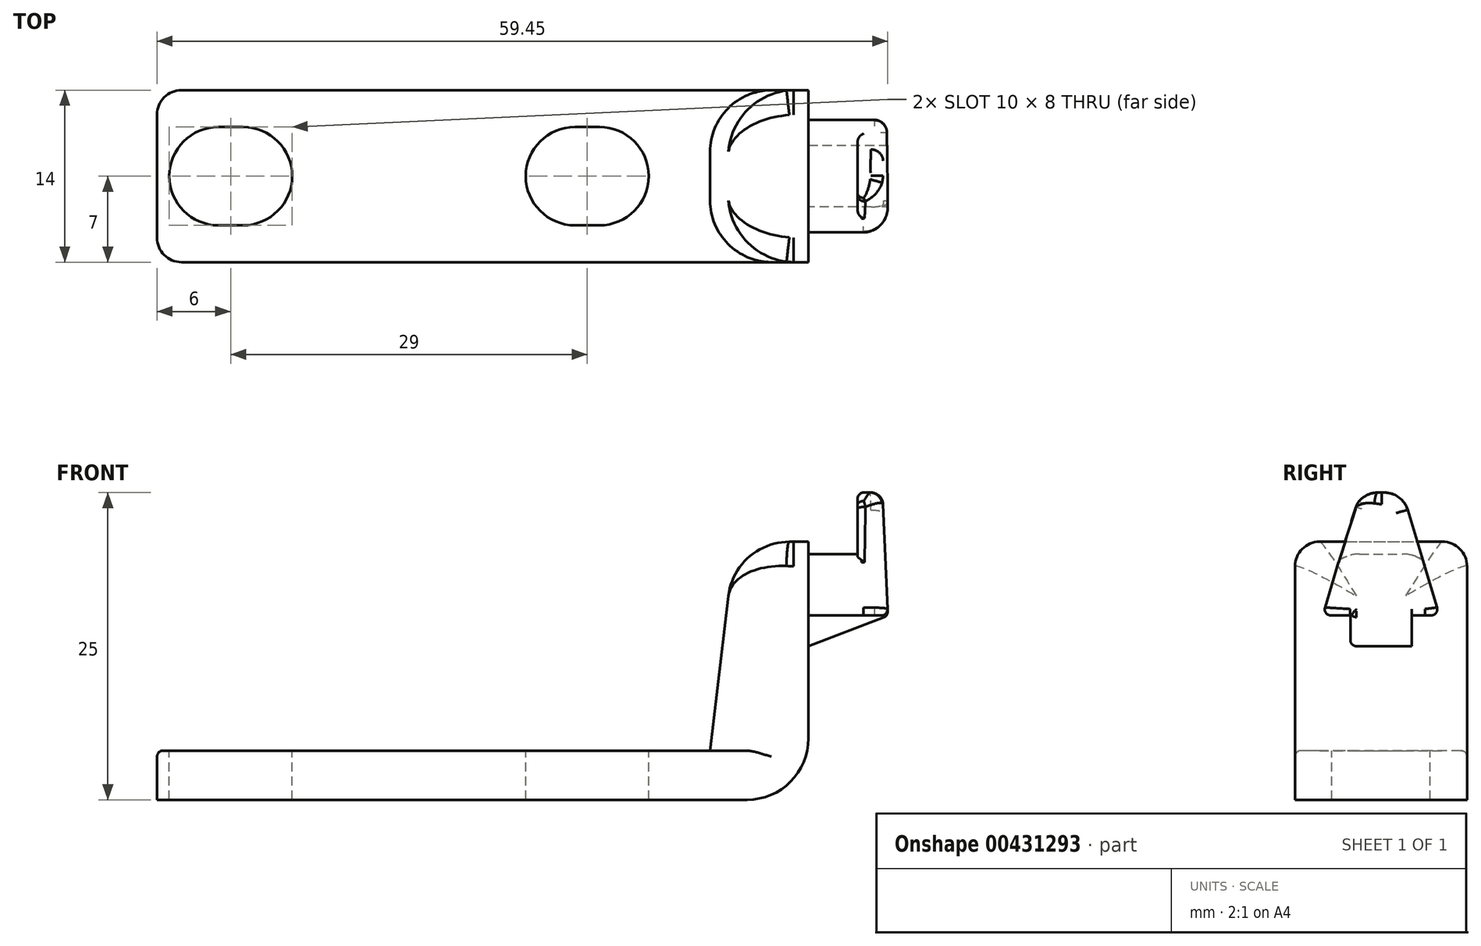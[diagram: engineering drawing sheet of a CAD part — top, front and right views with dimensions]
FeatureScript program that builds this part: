
annotation { "Feature Type Name" : "Feature", "Feature Type Description" : "" }
export const myFeature = defineFeature(function(context is Context, id is Id, definition is map)
    precondition{}
    {
        {
            var Q0;
            Q0=qCreatedBy(makeId("Front.planeOp"),FACE);
            var sketch = newSketch(context, id + "F0", { "sketchPlane" : qUnion([Q0])});
            skLineSegment(sketch, "E0.bottom", {"start": v(-32.49, -4) * mm, "end": v(20.51, -4) * mm});
            skLineSegment(sketch, "E0.top", {"start": v(-32.49, 0) * mm, "end": v(20.51, 0) * mm});
            skLineSegment(sketch, "E0.left", {"start": v(-32.49, -4) * mm, "end": v(-32.49, 0) * mm});
            skLineSegment(sketch, "E0.right", {"start": v(20.51, -4) * mm, "end": v(20.51, 0) * mm});
            skLineSegment(sketch, "E1", {"start": v(20.51, 0) * mm, "end": v(20.51, 17) * mm});
            skLineSegment(sketch, "E2", {"start": v(20.51, 17) * mm, "end": v(14.51, 17) * mm});
            skLineSegment(sketch, "E3", {"start": v(14.51, 17) * mm, "end": v(12.51, 0) * mm});
            skLineSegment(sketch, "E4", {"start": v(12.51, 0) * mm, "end": v(20.51, 0) * mm});
            skLineSegment(sketch, "E5.bottom", {"start": v(20.51, 16) * mm, "end": v(24.51, 16) * mm});
            skLineSegment(sketch, "E5.top", {"start": v(20.51, 11) * mm, "end": v(24.51, 11) * mm});
            skLineSegment(sketch, "E5.left", {"start": v(20.51, 16) * mm, "end": v(20.51, 11) * mm});
            skLineSegment(sketch, "E5.right", {"start": v(24.51, 16) * mm, "end": v(24.51, 11) * mm});
            skLineSegment(sketch, "E6.bottom", {"start": v(24.51, 11) * mm, "end": v(27.01, 11) * mm});
            skLineSegment(sketch, "E6.top", {"start": v(24.51, 21) * mm, "end": v(27.01, 21) * mm});
            skLineSegment(sketch, "E6.left", {"start": v(24.51, 11) * mm, "end": v(24.51, 21) * mm});
            skLineSegment(sketch, "E6.right", {"start": v(27.01, 11) * mm, "end": v(27.01, 21) * mm});
            skArc(sketch, "E7", {"start": v(27.01, 11) * mm, "mid": v(26.28, 9.23) * mm, "end": v(24.51, 8.5) * mm});
            skLineSegment(sketch, "E8", {"start": v(24.51, 8.5) * mm, "end": v(20.51, 8.5) * mm});
            skSolve(sketch);
        }
        {
            var Q0;
            {var subQ0=sQuery(id+"F0.wireOp",EDGE,"E2");Q0=makeQuery(id+"F0.imprint","IMPRINT",FACE,{"disambiguationData":[TD([[makeQuery(id+"F0.imprint","IMPRINT",EDGE,{"derivedFrom":subQ0}),1.0]])]});}
            var Q1;
            Q1=makeQuery(id+"F0.imprint","IMPRINT",FACE,{"disambiguationData":[TD([[makeQuery(id+"F0.imprint","IMPRINT",EDGE,{"derivedFrom":sQuery(id+"F0.wireOp",EDGE,"E0.bottom")}),1.0]])]});
            extrude(context, id + "F1", {"entities" : qUnion([Q0, Q1]), "endBound" : BoundingType.SYMMETRIC, "depth" : 14 * mm, "offsetDistance" : 25 * mm});
        }
        {
            var Q0;
            {var subQ0=sQuery(id+"F0.wireOp",EDGE,"E5.bottom");Q0=makeQuery(id+"F0.imprint","IMPRINT",FACE,{"disambiguationData":[TD([[makeQuery(id+"F0.imprint","IMPRINT",EDGE,{"derivedFrom":subQ0}),-1.0]])]});}
            extrude(context, id + "F2", {"entities" : qUnion([Q0]), "operationType" : NewBodyOperationType.ADD, "endBound" : BoundingType.SYMMETRIC, "depth" : 9.5 * mm, "offsetDistance" : 25 * mm});
        }
        {
            var Q0;
            {var subQ3=sQuery(id+"F0.wireOp",EDGE,"E6.bottom");Q0=makeQuery(id+"F0.imprint","IMPRINT",FACE,{"disambiguationData":[TD([[makeQuery(id+"F0.imprint","IMPRINT",EDGE,{"derivedFrom":subQ3}),1.0]])]});}
            extrude(context, id + "F3", {"entities" : qUnion([Q0]), "operationType" : NewBodyOperationType.ADD, "endBound" : BoundingType.SYMMETRIC, "depth" : 9.5 * mm, "offsetDistance" : 25 * mm});
        }
        {
            var Q0;
            {var subQ0=sQuery(id+"F0.wireOp",EDGE,"E5.top");Q0=makeQuery(id+"F0.imprint","IMPRINT",FACE,{"disambiguationData":[TD([[makeQuery(id+"F0.imprint","IMPRINT",EDGE,{"derivedFrom":subQ0}),-1.0]])]});}
            extrude(context, id + "F4", {"entities" : qUnion([Q0]), "operationType" : NewBodyOperationType.ADD, "endBound" : BoundingType.SYMMETRIC, "depth" : 5 * mm, "offsetDistance" : 25 * mm});
        }
        {
            var Q0;
            Q0=makeQuery(id+"F1.opExtrude","CAP_EDGE",EDGE,{"disambiguationData":[OSD([sQuery(id+"F0.wireOp",EDGE,"E0.left")])],"isStart":true});
            var Q1;
            Q1=makeQuery(id+"F1.opExtrude","CAP_EDGE",EDGE,{"disambiguationData":[OSD([sQuery(id+"F0.wireOp",EDGE,"E0.left")])],"isStart":false});
            fillet(context, id + "F5", {"entities" : qUnion([Q0, Q1]), "radius" : 2 * mm, "tangentPropagation" : true, "allowEdgeOverflow" : false});
        }
        {
            var Q0;
            Q0=makeQuery(id+"F1.opExtrude","CAP_EDGE",EDGE,{"disambiguationData":[OSD([sQuery(id+"F0.wireOp",EDGE,"E2")])],"isStart":true});
            var Q1;
            Q1=makeQuery(id+"F1.opExtrude","CAP_EDGE",EDGE,{"disambiguationData":[OSD([sQuery(id+"F0.wireOp",EDGE,"E2")])],"isStart":false});
            fillet(context, id + "F6", {"entities" : qUnion([Q0, Q1]), "radius" : 2 * mm, "tangentPropagation" : true, "allowEdgeOverflow" : false});
        }
        {
            var Q0;
            Q0=makeQuery(id+"F2.opExtrude","CAP_EDGE",EDGE,{"disambiguationData":[OSD([sQuery(id+"F0.wireOp",EDGE,"E5.bottom")])],"isStart":true});
            var Q1;
            Q1=makeQuery(id+"F2.opExtrude","CAP_EDGE",EDGE,{"disambiguationData":[OSD([sQuery(id+"F0.wireOp",EDGE,"E5.bottom")])],"isStart":false});
            fillet(context, id + "F7", {"entities" : qUnion([Q0, Q1]), "radius" : 3 * mm, "tangentPropagation" : true, "allowEdgeOverflow" : false});
        }
        {
            var Q0;
            Q0=makeQuery(id+"F3.opExtrude","CAP_EDGE",EDGE,{"disambiguationData":[OSD([sQuery(id+"F0.wireOp",EDGE,"E6.top")])],"isStart":false});
            var Q1;
            Q1=makeQuery(id+"F3.opExtrude","CAP_EDGE",EDGE,{"disambiguationData":[OSD([sQuery(id+"F0.wireOp",EDGE,"E6.top")])],"isStart":true});
            fillet(context, id + "F8", {"entities" : qUnion([Q0, Q1]), "radius" : 3 * mm, "tangentPropagation" : true, "allowEdgeOverflow" : false});
        }
        {
            var Q0;
            Q0=qCreatedBy(makeId("Top.planeOp"),FACE);
            var sketch = newSketch(context, id + "F9", { "sketchPlane" : qUnion([Q0])});
            skLineSegment(sketch, "E9", {"start": v(1.51, 0) * mm, "end": v(3.51, 0) * mm});
            skArc(sketch, "E10.0.startCap", {"start": v(1.51, -4) * mm, "mid": v(-2.49, 0) * mm, "end": v(1.51, 4) * mm});
            skArc(sketch, "E10.0.endCap", {"start": v(3.51, 4) * mm, "mid": v(7.51, 0) * mm, "end": v(3.51, -4) * mm});
            skLineSegment(sketch, "E10.0.left", {"start": v(1.51, 4) * mm, "end": v(3.51, 4) * mm});
            skLineSegment(sketch, "E10.0.right", {"start": v(1.51, -4) * mm, "end": v(3.51, -4) * mm});
            skLineSegment(sketch, "E11", {"start": v(-27.49, 0) * mm, "end": v(-25.49, 0) * mm});
            skArc(sketch, "E12.0.startCap", {"start": v(-27.49, -4) * mm, "mid": v(-31.49, 0) * mm, "end": v(-27.49, 4) * mm});
            skArc(sketch, "E12.0.endCap", {"start": v(-25.49, 4) * mm, "mid": v(-21.49, 0) * mm, "end": v(-25.49, -4) * mm});
            skLineSegment(sketch, "E12.0.left", {"start": v(-27.49, 4) * mm, "end": v(-25.49, 4) * mm});
            skLineSegment(sketch, "E12.0.right", {"start": v(-27.49, -4) * mm, "end": v(-25.49, -4) * mm});
            skSolve(sketch);
        }
        {
            var Q0;
            Q0 = qSketchRegion(id + "F9", true);
            var Q1;
            Q1 = qSketchRegion(id + "FCVwkmBDjQpbv9k_1", true);
            extrude(context, id + "F10", {"entities" : qUnion([Q0, Q1]), "operationType" : NewBodyOperationType.REMOVE, "endBound" : BoundingType.THROUGH_ALL, "oppositeDirection" : true, "depth" : 25 * mm, "offsetDistance" : 25 * mm});
        }
        {
            var Q0;
            Q0=makeQuery(id+"F3.opExtrude","SWEPT_FACE",FACE,{"disambiguationData":[OSD([sQuery(id+"F0.wireOp",EDGE,"E6.right")])]});
            var sketch = newSketch(context, id + "F11", { "sketchPlane" : qUnion([Q0])});
            skLineSegment(sketch, "E13", {"start": v(-4.75, 11) * mm, "end": v(-1.75, 21) * mm});
            skLineSegment(sketch, "E14", {"start": v(4.75, 11) * mm, "end": v(1.75, 21) * mm});
            skSolve(sketch);
        }
        {
            var Q0;
            Q0=makeQuery(id+"F11.imprint","IMPRINT",FACE,{"disambiguationData":[TD([[makeQuery(id+"F11.imprint","IMPRINT",EDGE,{"derivedFrom":sQuery(id+"F11.wireOp",EDGE,"E14")}),-1.0]])]});
            var Q1;
            Q1=makeQuery(id+"F11.imprint","IMPRINT",FACE,{"disambiguationData":[TD([[makeQuery(id+"F11.imprint","IMPRINT",EDGE,{"derivedFrom":sQuery(id+"F11.wireOp",EDGE,"E13")}),1.0]])]});
            extrude(context, id + "F12", {"entities" : qUnion([Q0, Q1]), "operationType" : NewBodyOperationType.REMOVE, "oppositeDirection" : true, "depth" : 6.5 * mm, "offsetDistance" : 25 * mm});
        }
        {
            var Q0;
            Q0=makeQuery(id+"F12.boolean.opBoolean","COPY",FACE,{"derivedFrom":makeQuery(id+"F12.opExtrude","SWEPT_FACE",FACE,{"disambiguationData":[OSD([sQuery(id+"F11.wireOp",EDGE,"E13")])]})});
            var sketch = newSketch(context, id + "F13", { "sketchPlane" : qUnion([Q0])});
            skLineSegment(sketch, "E15", {"start": v(27.01, 9.17) * mm, "end": v(27.01, 21.8) * mm});
            skLineSegment(sketch, "E16", {"start": v(27.01, 21.8) * mm, "end": v(26.46, 21.8) * mm});
            skLineSegment(sketch, "E17", {"start": v(26.46, 21.8) * mm, "end": v(27.01, 9.17) * mm});
            skSolve(sketch);
        }
        {
            var Q0;
            {var subQ4=sQuery(id+"F13.wireOp",EDGE,"E16");Q0=makeQuery(id+"F13.imprint","IMPRINT",FACE,{"disambiguationData":[TD([[makeQuery(id+"F13.imprint","IMPRINT",EDGE,{"derivedFrom":subQ4}),1.0]])]});}
            var Q1;
            {var subQ1=sQuery(id+"F13.wireOp",EDGE,"E15");var subQ2=sQuery(id+"F11.wireOp",EDGE,"E13");var subQ3=sQuery(id+"F0.wireOp",EDGE,"E6.right");var subQ6=sQuery(id+"F0.wireOp",EDGE,"E6.top");var subQ7=makeQuery(id+"F12.boolean.opBoolean","MERGE",EDGE,{"derivedFrom":[makeQuery(id+"F8.opFillet","BLEND_EDGE",EDGE,{"blendedFrom":[makeQuery(id+"F3.opExtrude","CAP_EDGE",EDGE,{"disambiguationData":[OSD([subQ6])],"isStart":false}),makeQuery(id+"F3.opExtrude","SWEPT_FACE",FACE,{"disambiguationData":[OSD([subQ6])]})],"blendedInto":[makeQuery(id+"F3.opExtrude","SWEPT_FACE",FACE,{"disambiguationData":[OSD([subQ6])]})]}),makeQuery(id+"F12.opExtrude","SWEPT_EDGE",EDGE,{"disambiguationData":[OSD([subQ6,subQ3,subQ2])]})]});var subQ8=makeQuery(id+"F13.imprint","INTERSECT",VERTEX,{"derivedFrom":[subQ7,subQ1]});Q1=makeQuery(id+"F13.imprint","IMPRINT",FACE,{"disambiguationData":[TD([[makeQuery(id+"F13.imprint","IMPRINT",EDGE,{"disambiguationData":[TD([[subQ8,1.0]])],"derivedFrom":subQ1}),1.0]])]});}
            extrude(context, id + "F14", {"entities" : qUnion([Q0, Q1]), "operationType" : NewBodyOperationType.REMOVE, "oppositeDirection" : true, "depth" : 25 * mm, "offsetDistance" : 25 * mm});
        }
        {
            var Q0;
            Q0=makeQuery(id+"F14.boolean.opBoolean","INTERSECT",EDGE,{"derivedFrom":[makeQuery(id+"F12.boolean.opBoolean","COPY",FACE,{"derivedFrom":makeQuery(id+"F12.opExtrude","SWEPT_FACE",FACE,{"disambiguationData":[OSD([sQuery(id+"F11.wireOp",EDGE,"E14")])]})}),makeQuery(id+"F14.opExtrude","SWEPT_FACE",FACE,{"disambiguationData":[OSD([sQuery(id+"F13.wireOp",EDGE,"E17")])]})]});
            var Q1;
            Q1=makeQuery(id+"F14.boolean.opBoolean","INTERSECT",EDGE,{"derivedFrom":[makeQuery(id+"F3.opExtrude","SWEPT_FACE",FACE,{"disambiguationData":[OSD([sQuery(id+"F0.wireOp",EDGE,"E6.top")])]}),makeQuery(id+"F14.opExtrude","SWEPT_FACE",FACE,{"disambiguationData":[OSD([sQuery(id+"F13.wireOp",EDGE,"E17")])]})]});
            var Q2;
            Q2=makeQuery(id+"F14.boolean.opBoolean","COPY",EDGE,{"derivedFrom":makeQuery(id+"F14.opExtrude","CAP_EDGE",EDGE,{"disambiguationData":[OSD([sQuery(id+"F13.wireOp",EDGE,"E17")])],"isStart":true})});
            fillet(context, id + "F15", {"entities" : qUnion([Q0, Q1, Q2]), "radius" : 1 * mm, "tangentPropagation" : true, "allowEdgeOverflow" : false});
        }
        {
            var Q0;
            {var subQ0=sQuery(id+"F0.wireOp",EDGE,"E6.top");Q0=makeQuery(id+"F12.boolean.opBoolean","MERGE",EDGE,{"derivedFrom":[makeQuery(id+"F8.opFillet","BLEND_EDGE",EDGE,{"blendedFrom":[makeQuery(id+"F3.opExtrude","CAP_EDGE",EDGE,{"disambiguationData":[OSD([subQ0])],"isStart":false}),makeQuery(id+"F3.opExtrude","SWEPT_FACE",FACE,{"disambiguationData":[OSD([subQ0])]})],"blendedInto":[makeQuery(id+"F3.opExtrude","SWEPT_FACE",FACE,{"disambiguationData":[OSD([subQ0])]})]}),makeQuery(id+"F12.opExtrude","SWEPT_EDGE",EDGE,{"disambiguationData":[OSD([subQ0,sQuery(id+"F0.wireOp",EDGE,"E6.right"),sQuery(id+"F11.wireOp",EDGE,"E13")])]})]});}
            var Q1;
            {var subQ0=sQuery(id+"F0.wireOp",EDGE,"E6.top");Q1=makeQuery(id+"F12.boolean.opBoolean","MERGE",EDGE,{"derivedFrom":[makeQuery(id+"F8.opFillet","BLEND_EDGE",EDGE,{"blendedFrom":[makeQuery(id+"F3.opExtrude","CAP_EDGE",EDGE,{"disambiguationData":[OSD([subQ0])],"isStart":true}),makeQuery(id+"F3.opExtrude","SWEPT_FACE",FACE,{"disambiguationData":[OSD([subQ0])]})],"blendedInto":[makeQuery(id+"F3.opExtrude","SWEPT_FACE",FACE,{"disambiguationData":[OSD([subQ0])]})]}),makeQuery(id+"F12.opExtrude","SWEPT_EDGE",EDGE,{"disambiguationData":[OSD([subQ0,sQuery(id+"F0.wireOp",EDGE,"E6.right"),sQuery(id+"F11.wireOp",EDGE,"E14")])]})]});}
            fillet(context, id + "F16", {"entities" : qUnion([Q0, Q1]), "radius" : 2 * mm, "tangentPropagation" : true, "allowEdgeOverflow" : false});
        }
        {
            var Q0;
            Q0=makeQuery(id+"F4.opExtrude","CAP_FACE",FACE,{"disambiguationData":[OSD([sQuery(id+"F0.wireOp",EDGE,"E1"),sQuery(id+"F0.wireOp",EDGE,"E5.top"),sQuery(id+"F0.wireOp",EDGE,"E6.bottom"),sQuery(id+"F0.wireOp",EDGE,"E7"),sQuery(id+"F0.wireOp",EDGE,"E8")])],"isStart":true});
            var sketch = newSketch(context, id + "F17", { "sketchPlane" : qUnion([Q0])});
            skLineSegment(sketch, "E18", {"start": v(-20.51, 8.5) * mm, "end": v(-27.01, 11) * mm});
            skLineSegment(sketch, "E19", {"start": v(-27.01, 11) * mm, "end": v(-27.01, 8.31) * mm});
            skLineSegment(sketch, "E20", {"start": v(-27.01, 8.31) * mm, "end": v(-20.51, 8.5) * mm});
            skSolve(sketch);
        }
        {
            var Q0;
            {var subQ1=sQuery(id+"F17.wireOp",EDGE,"E19");Q0=makeQuery(id+"F17.imprint","IMPRINT",FACE,{"disambiguationData":[TD([[makeQuery(id+"F17.imprint","IMPRINT",EDGE,{"derivedFrom":subQ1}),1.0]])]});}
            var Q1;
            {var subQ2=sQuery(id+"F0.wireOp",EDGE,"E8");var subQ3=makeQuery(id+"F4.opExtrude","CAP_EDGE",EDGE,{"disambiguationData":[OSD([subQ2])],"isStart":true});Q1=makeQuery(id+"F17.imprint","IMPRINT",FACE,{"disambiguationData":[TD([[makeQuery(id+"F17.imprint","IMPRINT",EDGE,{"derivedFrom":subQ3}),1.0]])]});}
            extrude(context, id + "F18", {"entities" : qUnion([Q0, Q1]), "operationType" : NewBodyOperationType.REMOVE, "oppositeDirection" : true, "depth" : 25 * mm, "offsetDistance" : 25 * mm});
        }
        {
            var Q0;
            Q0=makeQuery(id+"F12.boolean.opBoolean","INTERSECT",EDGE,{"derivedFrom":[makeQuery(id+"F3.opExtrude","SWEPT_FACE",FACE,{"disambiguationData":[OSD([sQuery(id+"F0.wireOp",EDGE,"E6.left")])]}),makeQuery(id+"F12.opExtrude","SWEPT_FACE",FACE,{"disambiguationData":[OSD([sQuery(id+"F11.wireOp",EDGE,"E14")])]})]});
            var Q1;
            {var subQ0=sQuery(id+"F0.wireOp",EDGE,"E6.top");Q1=makeQuery(id+"F16.opFillet","BLEND_EDGE",EDGE,{"blendedFrom":[makeQuery(id+"F12.boolean.opBoolean","MERGE",EDGE,{"derivedFrom":[makeQuery(id+"F8.opFillet","BLEND_EDGE",EDGE,{"blendedFrom":[makeQuery(id+"F3.opExtrude","CAP_EDGE",EDGE,{"disambiguationData":[OSD([subQ0])],"isStart":true}),makeQuery(id+"F3.opExtrude","SWEPT_FACE",FACE,{"disambiguationData":[OSD([subQ0])]})],"blendedInto":[makeQuery(id+"F3.opExtrude","SWEPT_FACE",FACE,{"disambiguationData":[OSD([subQ0])]})]}),makeQuery(id+"F12.opExtrude","SWEPT_EDGE",EDGE,{"disambiguationData":[OSD([subQ0,sQuery(id+"F0.wireOp",EDGE,"E6.right"),sQuery(id+"F11.wireOp",EDGE,"E14")])]})]}),makeQuery(id+"F3.opExtrude","SWEPT_FACE",FACE,{"disambiguationData":[OSD([sQuery(id+"F0.wireOp",EDGE,"E6.left")])]})],"blendedInto":[makeQuery(id+"F3.opExtrude","SWEPT_FACE",FACE,{"disambiguationData":[OSD([sQuery(id+"F0.wireOp",EDGE,"E6.left")])]})]});}
            var Q2;
            {var subQ0=sQuery(id+"F0.wireOp",EDGE,"E6.top");Q2=makeQuery(id+"F16.opFillet","BLEND_EDGE",EDGE,{"blendedFrom":[makeQuery(id+"F12.boolean.opBoolean","MERGE",EDGE,{"derivedFrom":[makeQuery(id+"F8.opFillet","BLEND_EDGE",EDGE,{"blendedFrom":[makeQuery(id+"F3.opExtrude","CAP_EDGE",EDGE,{"disambiguationData":[OSD([subQ0])],"isStart":false}),makeQuery(id+"F3.opExtrude","SWEPT_FACE",FACE,{"disambiguationData":[OSD([subQ0])]})],"blendedInto":[makeQuery(id+"F3.opExtrude","SWEPT_FACE",FACE,{"disambiguationData":[OSD([subQ0])]})]}),makeQuery(id+"F12.opExtrude","SWEPT_EDGE",EDGE,{"disambiguationData":[OSD([subQ0,sQuery(id+"F0.wireOp",EDGE,"E6.right"),sQuery(id+"F11.wireOp",EDGE,"E13")])]})]}),makeQuery(id+"F3.opExtrude","SWEPT_FACE",FACE,{"disambiguationData":[OSD([sQuery(id+"F0.wireOp",EDGE,"E6.left")])]})],"blendedInto":[makeQuery(id+"F3.opExtrude","SWEPT_FACE",FACE,{"disambiguationData":[OSD([sQuery(id+"F0.wireOp",EDGE,"E6.left")])]})]});}
            var Q3;
            Q3=makeQuery(id+"F12.boolean.opBoolean","INTERSECT",EDGE,{"derivedFrom":[makeQuery(id+"F3.opExtrude","SWEPT_FACE",FACE,{"disambiguationData":[OSD([sQuery(id+"F0.wireOp",EDGE,"E6.left")])]}),makeQuery(id+"F12.opExtrude","SWEPT_FACE",FACE,{"disambiguationData":[OSD([sQuery(id+"F11.wireOp",EDGE,"E13")])]})]});
            var Q4;
            Q4=makeQuery(id+"F3.opExtrude","SWEPT_EDGE",EDGE,{"disambiguationData":[OSD([sQuery(id+"F0.wireOp",EDGE,"E6.top"),sQuery(id+"F0.wireOp",EDGE,"E6.left")])]});
            fillet(context, id + "F19", {"entities" : qUnion([Q0, Q1, Q2, Q3, Q4]), "radius" : 0.5 * mm, "tangentPropagation" : true, "allowEdgeOverflow" : false});
        }
        {
            var Q0;
            {var subQ0=sQuery(id+"F0.wireOp",EDGE,"E5.bottom");Q0=makeQuery(id+"F12.boolean.opBoolean","INTERSECT",EDGE,{"derivedFrom":[makeQuery(id+"F7.opFillet","BLEND_FACE",FACE,{"disambiguationData":[OSD([subQ0]),TDD([makeQuery(id+"F2.opExtrude","CAP_EDGE",EDGE,{"disambiguationData":[OSD([subQ0])],"isStart":false})])]}),makeQuery(id+"F12.opExtrude","SWEPT_FACE",FACE,{"disambiguationData":[OSD([sQuery(id+"F11.wireOp",EDGE,"E13")])]})]});}
            var Q1;
            {var subQ0=sQuery(id+"F0.wireOp",EDGE,"E6.bottom");Q1=makeQuery(id+"F12.boolean.opBoolean","MERGE",EDGE,{"derivedFrom":[makeQuery(id+"F3.boolean.opBoolean","MERGE",EDGE,{"derivedFrom":[makeQuery(id+"F2.opExtrude","CAP_EDGE",EDGE,{"disambiguationData":[OSD([sQuery(id+"F0.wireOp",EDGE,"E5.top")])],"isStart":false}),makeQuery(id+"F3.opExtrude","CAP_EDGE",EDGE,{"disambiguationData":[OSD([subQ0])],"isStart":false})]}),makeQuery(id+"F12.opExtrude","SWEPT_EDGE",EDGE,{"disambiguationData":[OSD([subQ0,sQuery(id+"F0.wireOp",EDGE,"E6.right"),sQuery(id+"F0.wireOp",EDGE,"E7"),sQuery(id+"F11.wireOp",EDGE,"E13")])]})]});}
            fillet(context, id + "F20", {"entities" : qUnion([Q0, Q1]), "radius" : 0.5 * mm, "tangentPropagation" : true, "allowEdgeOverflow" : false});
        }
        {
            var Q0;
            {var subQ0=sQuery(id+"F0.wireOp",EDGE,"E5.bottom");Q0=makeQuery(id+"F12.boolean.opBoolean","INTERSECT",EDGE,{"derivedFrom":[makeQuery(id+"F7.opFillet","BLEND_FACE",FACE,{"disambiguationData":[OSD([subQ0]),TDD([makeQuery(id+"F2.opExtrude","CAP_EDGE",EDGE,{"disambiguationData":[OSD([subQ0])],"isStart":true})])]}),makeQuery(id+"F12.opExtrude","SWEPT_FACE",FACE,{"disambiguationData":[OSD([sQuery(id+"F11.wireOp",EDGE,"E14")])]})]});}
            var Q1;
            {var subQ0=sQuery(id+"F0.wireOp",EDGE,"E6.bottom");Q1=makeQuery(id+"F12.boolean.opBoolean","MERGE",EDGE,{"derivedFrom":[makeQuery(id+"F3.boolean.opBoolean","MERGE",EDGE,{"derivedFrom":[makeQuery(id+"F2.opExtrude","CAP_EDGE",EDGE,{"disambiguationData":[OSD([sQuery(id+"F0.wireOp",EDGE,"E5.top")])],"isStart":true}),makeQuery(id+"F3.opExtrude","CAP_EDGE",EDGE,{"disambiguationData":[OSD([subQ0])],"isStart":true})]}),makeQuery(id+"F12.opExtrude","SWEPT_EDGE",EDGE,{"disambiguationData":[OSD([subQ0,sQuery(id+"F0.wireOp",EDGE,"E6.right"),sQuery(id+"F0.wireOp",EDGE,"E7"),sQuery(id+"F11.wireOp",EDGE,"E14")])]})]});}
            fillet(context, id + "F21", {"entities" : qUnion([Q0, Q1]), "radius" : 0.5 * mm, "tangentPropagation" : true, "allowEdgeOverflow" : false});
        }
        {
            var Q0;
            Q0=makeQuery(id+"F18.boolean.opBoolean","COPY",EDGE,{"derivedFrom":makeQuery(id+"F18.opExtrude","CAP_EDGE",EDGE,{"disambiguationData":[OSD([sQuery(id+"F17.wireOp",EDGE,"E18")])],"isStart":true})});
            var Q1;
            Q1=makeQuery(id+"F18.boolean.opBoolean","INTERSECT",EDGE,{"derivedFrom":[makeQuery(id+"F4.opExtrude","CAP_FACE",FACE,{"disambiguationData":[OSD([sQuery(id+"F0.wireOp",EDGE,"E1"),sQuery(id+"F0.wireOp",EDGE,"E5.top"),sQuery(id+"F0.wireOp",EDGE,"E6.bottom"),sQuery(id+"F0.wireOp",EDGE,"E7"),sQuery(id+"F0.wireOp",EDGE,"E8")])],"isStart":false}),makeQuery(id+"F18.opExtrude","SWEPT_FACE",FACE,{"disambiguationData":[OSD([sQuery(id+"F17.wireOp",EDGE,"E18")])]})]});
            fillet(context, id + "F22", {"entities" : qUnion([Q0, Q1]), "radius" : 0.5 * mm, "tangentPropagation" : true, "allowEdgeOverflow" : false});
        }
        {
            var Q0;
            Q0=makeQuery(id+"F18.boolean.opBoolean","INTERSECT",EDGE,{"derivedFrom":[makeQuery(id+"F14.boolean.opBoolean","COPY",FACE,{"derivedFrom":makeQuery(id+"F14.opExtrude","SWEPT_FACE",FACE,{"disambiguationData":[OSD([sQuery(id+"F13.wireOp",EDGE,"E17")])]})}),makeQuery(id+"F18.opExtrude","SWEPT_FACE",FACE,{"disambiguationData":[OSD([sQuery(id+"F17.wireOp",EDGE,"E18")])]})]});
            fillet(context, id + "F23", {"entities" : qUnion([Q0]), "radius" : 0.5 * mm, "tangentPropagation" : true, "allowEdgeOverflow" : false});
        }
        {
            var Q0;
            Q0=makeQuery(id+"F1.opExtrude","SWEPT_EDGE",EDGE,{"disambiguationData":[OSD([sQuery(id+"F0.wireOp",EDGE,"E0.bottom"),sQuery(id+"F0.wireOp",EDGE,"E0.right")])]});
            fillet(context, id + "F24", {"entities" : qUnion([Q0]), "radius" : 5 * mm, "tangentPropagation" : true, "allowEdgeOverflow" : false});
        }
        {
            var Q0;
            Q0=makeQuery(id+"F1.opExtrude","SWEPT_EDGE",EDGE,{"disambiguationData":[OSD([sQuery(id+"F0.wireOp",EDGE,"E2"),sQuery(id+"F0.wireOp",EDGE,"E3")])]});
            var Q1;
            Q1=makeQuery(id+"F6.opFillet","BLEND_EDGE",EDGE,{"blendedFrom":[makeQuery(id+"F1.opExtrude","CAP_EDGE",EDGE,{"disambiguationData":[OSD([sQuery(id+"F0.wireOp",EDGE,"E2")])],"isStart":false}),makeQuery(id+"F1.opExtrude","SWEPT_FACE",FACE,{"disambiguationData":[OSD([sQuery(id+"F0.wireOp",EDGE,"E3")])]})],"blendedInto":[makeQuery(id+"F1.opExtrude","SWEPT_FACE",FACE,{"disambiguationData":[OSD([sQuery(id+"F0.wireOp",EDGE,"E3")])]})]});
            var Q2;
            Q2=makeQuery(id+"F6.opFillet","BLEND_EDGE",EDGE,{"blendedFrom":[makeQuery(id+"F1.opExtrude","CAP_EDGE",EDGE,{"disambiguationData":[OSD([sQuery(id+"F0.wireOp",EDGE,"E2")])],"isStart":true}),makeQuery(id+"F1.opExtrude","SWEPT_FACE",FACE,{"disambiguationData":[OSD([sQuery(id+"F0.wireOp",EDGE,"E3")])]})],"blendedInto":[makeQuery(id+"F1.opExtrude","SWEPT_FACE",FACE,{"disambiguationData":[OSD([sQuery(id+"F0.wireOp",EDGE,"E3")])]})]});
            var Q3;
            Q3=makeQuery(id+"F1.opExtrude","CAP_EDGE",EDGE,{"disambiguationData":[OSD([sQuery(id+"F0.wireOp",EDGE,"E3")])],"isStart":true});
            var Q4;
            Q4=makeQuery(id+"F1.opExtrude","CAP_EDGE",EDGE,{"disambiguationData":[OSD([sQuery(id+"F0.wireOp",EDGE,"E3")])],"isStart":false});
            fillet(context, id + "F25", {"entities" : qUnion([Q0, Q1, Q2, Q3, Q4]), "radius" : 5 * mm, "tangentPropagation" : true, "allowEdgeOverflow" : false});
        }
        {
            var Q0;
            Q0=makeQuery(id+"F1.opExtrude","CAP_EDGE",EDGE,{"disambiguationData":[OSD([sQuery(id+"F0.wireOp",EDGE,"E0.top")])],"isStart":false});
            var Q1;
            Q1=makeQuery(id+"F5.opFillet","BLEND_EDGE",EDGE,{"blendedFrom":[makeQuery(id+"F1.opExtrude","CAP_EDGE",EDGE,{"disambiguationData":[OSD([sQuery(id+"F0.wireOp",EDGE,"E0.left")])],"isStart":false}),makeQuery(id+"F1.opExtrude","SWEPT_FACE",FACE,{"disambiguationData":[OSD([sQuery(id+"F0.wireOp",EDGE,"E0.top")])]})],"blendedInto":[makeQuery(id+"F1.opExtrude","SWEPT_FACE",FACE,{"disambiguationData":[OSD([sQuery(id+"F0.wireOp",EDGE,"E0.top")])]})]});
            var Q2;
            Q2=makeQuery(id+"F1.opExtrude","SWEPT_EDGE",EDGE,{"disambiguationData":[OSD([sQuery(id+"F0.wireOp",EDGE,"E0.top"),sQuery(id+"F0.wireOp",EDGE,"E0.left")])]});
            var Q3;
            Q3=makeQuery(id+"F1.opExtrude","CAP_EDGE",EDGE,{"disambiguationData":[OSD([sQuery(id+"F0.wireOp",EDGE,"E0.top")])],"isStart":true});
            var Q4;
            Q4=makeQuery(id+"F5.opFillet","BLEND_EDGE",EDGE,{"blendedFrom":[makeQuery(id+"F1.opExtrude","CAP_EDGE",EDGE,{"disambiguationData":[OSD([sQuery(id+"F0.wireOp",EDGE,"E0.left")])],"isStart":true}),makeQuery(id+"F1.opExtrude","SWEPT_FACE",FACE,{"disambiguationData":[OSD([sQuery(id+"F0.wireOp",EDGE,"E0.top")])]})],"blendedInto":[makeQuery(id+"F1.opExtrude","SWEPT_FACE",FACE,{"disambiguationData":[OSD([sQuery(id+"F0.wireOp",EDGE,"E0.top")])]})]});
            fillet(context, id + "F26", {"entities" : qUnion([Q0, Q1, Q2, Q3, Q4]), "radius" : 0.5 * mm, "tangentPropagation" : true, "allowEdgeOverflow" : false});
        }
    });
